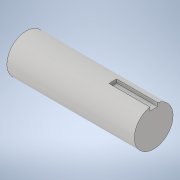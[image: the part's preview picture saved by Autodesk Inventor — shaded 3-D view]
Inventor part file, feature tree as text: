
AUTODESK INVENTOR PART (.ipt)
format: ipt  version: 2021 (Build 250183000, 183)  size: 105,472 bytes
history: native  units: in
note: dims shown in document units (in); Inventor stores cm internally (conversion verified against a paired STEP export)
features: extrude x2, sketch x2, plane x1
ambient origin geometry x8: Origin, YZ Plane, XZ Plane, XY Plane, X Axis, Y Axis, Z Axis, Center Point
bodies: Solid1 (feature_tree)
feature tree (5):
  extrude  "Extrusion1"  Depth=4.107in TaperAngle=0.0deg
  plane  "Work Plane1"
  extrude  "Extrusion9"  Depth=0.25in
  sketch  "Sketch1"  dims[d0=1.25in d1=4.107in d2=0.0in]
  sketch  "Sketch9"  dims[d11=-2.0535in d26=0.25in d27=0.125in d28=1.313in d29=0.0in]
